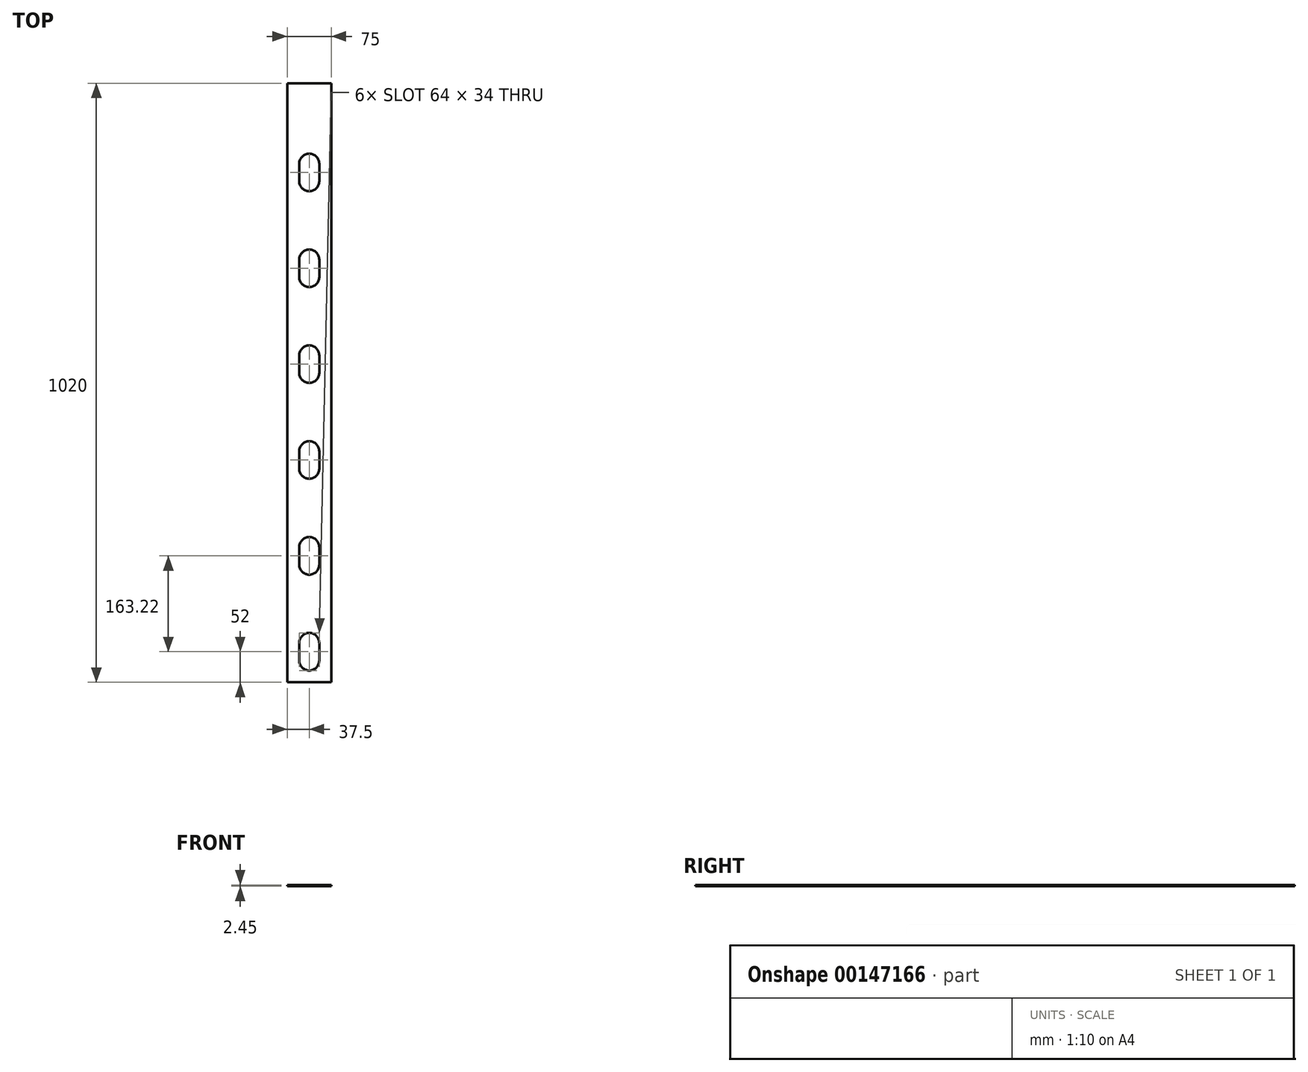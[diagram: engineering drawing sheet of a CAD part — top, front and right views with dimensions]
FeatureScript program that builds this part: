
annotation { "Feature Type Name" : "Feature", "Feature Type Description" : "" }
export const myFeature = defineFeature(function(context is Context, id is Id, definition is map)
    precondition{}
    {
        {
            var Q0;
            Q0=qCreatedBy(makeId("Top.planeOp"),FACE);
            var sketch = newSketch(context, id + "F0", { "sketchPlane" : qUnion([Q0])});
            skLineSegment(sketch, "E0.bottom", {"start": v(37.5, -510) * mm, "end": v(-37.5, -510) * mm});
            skLineSegment(sketch, "E0.top", {"start": v(37.5, 510) * mm, "end": v(-37.5, 510) * mm});
            skLineSegment(sketch, "E0.left", {"start": v(37.5, -510) * mm, "end": v(37.5, 510) * mm});
            skLineSegment(sketch, "E0.right", {"start": v(-37.5, -510) * mm, "end": v(-37.5, 510) * mm});
            skPoint(sketch, "E0.middle", {"position": v(0, 0) * mm});
            skPoint(sketch, "E1.center.orphan", {"position": v(22.25, -0.97) * mm});
            skArc(sketch, "E2", {"start": v(-17, -473) * mm, "mid": v(0, -490) * mm, "end": v(17, -473) * mm});
            skArc(sketch, "E3", {"start": v(17, -443) * mm, "mid": v(0, -426) * mm, "end": v(-17, -443) * mm});
            skLineSegment(sketch, "E4", {"start": v(-17, -443) * mm, "end": v(-17, -473) * mm});
            skLineSegment(sketch, "E5", {"start": v(17, -443) * mm, "end": v(17, -473) * mm});
            skArc(sketch, "E6", {"start": v(-17, -309.78) * mm, "mid": v(0, -326.78) * mm, "end": v(17, -309.78) * mm});
            skArc(sketch, "E7", {"start": v(17, -279.78) * mm, "mid": v(0, -262.78) * mm, "end": v(-17, -279.78) * mm});
            skLineSegment(sketch, "E8", {"start": v(-17, -279.78) * mm, "end": v(-17, -309.78) * mm});
            skLineSegment(sketch, "E9", {"start": v(17, -279.78) * mm, "end": v(17, -309.78) * mm});
            skArc(sketch, "E10", {"start": v(-17, -146.56) * mm, "mid": v(0, -163.56) * mm, "end": v(17, -146.56) * mm});
            skArc(sketch, "E11", {"start": v(17, -116.56) * mm, "mid": v(0, -99.56) * mm, "end": v(-17, -116.56) * mm});
            skLineSegment(sketch, "E12", {"start": v(-17, -116.56) * mm, "end": v(-17, -146.56) * mm});
            skLineSegment(sketch, "E13", {"start": v(17, -116.56) * mm, "end": v(17, -146.56) * mm});
            skArc(sketch, "E14", {"start": v(-17, 16.66) * mm, "mid": v(0, -0.34) * mm, "end": v(17, 16.66) * mm});
            skArc(sketch, "E15", {"start": v(17, 46.66) * mm, "mid": v(0, 63.66) * mm, "end": v(-17, 46.66) * mm});
            skLineSegment(sketch, "E16", {"start": v(-17, 46.66) * mm, "end": v(-17, 16.66) * mm});
            skLineSegment(sketch, "E17", {"start": v(17, 46.66) * mm, "end": v(17, 16.66) * mm});
            skArc(sketch, "E18", {"start": v(-17, 179.88) * mm, "mid": v(0, 162.88) * mm, "end": v(17, 179.88) * mm});
            skArc(sketch, "E19", {"start": v(17, 209.88) * mm, "mid": v(0, 226.88) * mm, "end": v(-17, 209.88) * mm});
            skLineSegment(sketch, "E20", {"start": v(-17, 209.88) * mm, "end": v(-17, 179.88) * mm});
            skLineSegment(sketch, "E21", {"start": v(17, 209.88) * mm, "end": v(17, 179.88) * mm});
            skArc(sketch, "E22", {"start": v(-17, 343.1) * mm, "mid": v(0, 326.1) * mm, "end": v(17, 343.1) * mm});
            skArc(sketch, "E23", {"start": v(17, 373.1) * mm, "mid": v(0, 390.1) * mm, "end": v(-17, 373.1) * mm});
            skLineSegment(sketch, "E24", {"start": v(-17, 373.1) * mm, "end": v(-17, 343.1) * mm});
            skLineSegment(sketch, "E25", {"start": v(17, 373.1) * mm, "end": v(17, 343.1) * mm});
            skSolve(sketch);
        }
        {
            var Q0;
            Q0=qSketchRegion(id+"F0",true);
            var Q1;
            Q1=makeQuery(id+"F0.imprint","IMPRINT",FACE,{"disambiguationData":[TD([[makeQuery(id+"F0.imprint","IMPRINT",EDGE,{"derivedFrom":sQuery(id+"F0.wireOp",EDGE,"E0.bottom")}),-1.0]])]});
            extrude(context, id + "F1", {"entities" : qUnion([Q0, Q1]), "depth" : 2.45 * mm});
        }
    });
